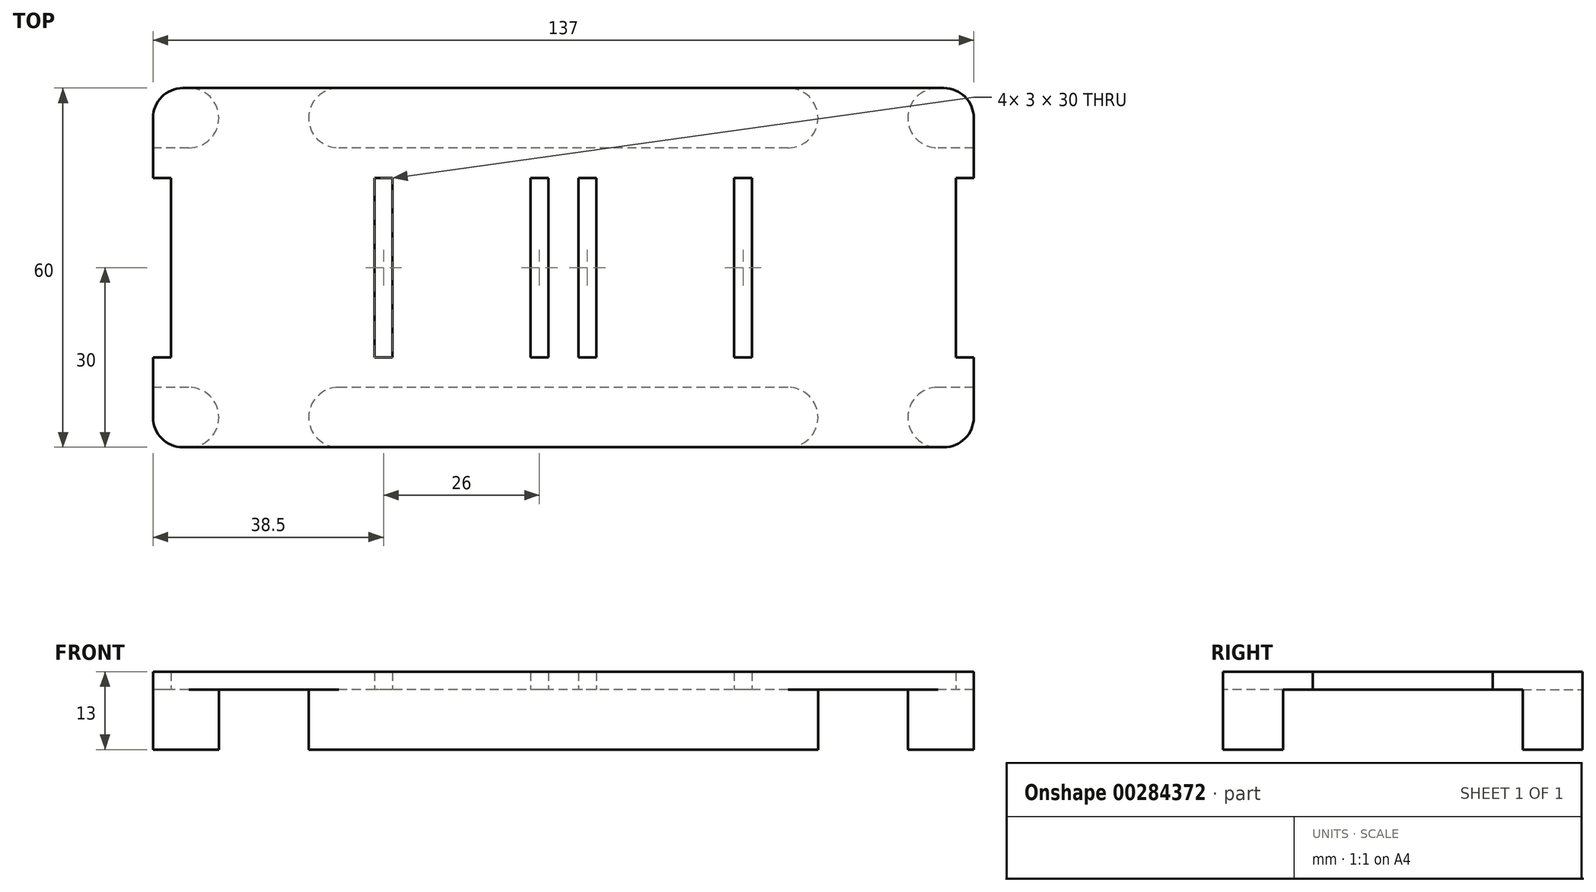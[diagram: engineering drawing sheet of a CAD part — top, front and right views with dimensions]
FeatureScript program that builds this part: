
annotation { "Feature Type Name" : "Feature", "Feature Type Description" : "" }
export const myFeature = defineFeature(function(context is Context, id is Id, definition is map)
    precondition{}
    {
        {
            var Q0;
            Q0=qCreatedBy(makeId("Top.planeOp"),FACE);
            var sketch = newSketch(context, id + "F0", { "sketchPlane" : qUnion([Q0])});
            skLineSegment(sketch, "E0.bottom", {"start": v(75, -30) * mm, "end": v(-75, -30) * mm});
            skLineSegment(sketch, "E0.top", {"start": v(75, 30) * mm, "end": v(-75, 30) * mm});
            skLineSegment(sketch, "E0.left", {"start": v(75, -30) * mm, "end": v(75, 30) * mm});
            skLineSegment(sketch, "E0.right", {"start": v(-75, -30) * mm, "end": v(-75, 30) * mm});
            skPoint(sketch, "E0.middle", {"position": v(0, 0) * mm});
            skSolve(sketch);
        }
        {
            var Q0;
            Q0 = qSketchRegion(id + "F0", true);
            extrude(context, id + "F1", {"entities" : qUnion([Q0]), "depth" : 3 * mm});
        }
        {
            var Q0;
            Q0=qCreatedBy(makeId("Top.planeOp"),FACE);
            var sketch = newSketch(context, id + "F2", { "sketchPlane" : qUnion([Q0])});
            skLineSegment(sketch, "E1.bottom", {"start": v(-2.5, -15) * mm, "end": v(-5.5, -15) * mm});
            skLineSegment(sketch, "E1.top", {"start": v(-2.5, 15) * mm, "end": v(-5.5, 15) * mm});
            skLineSegment(sketch, "E1.left", {"start": v(-2.5, -15) * mm, "end": v(-2.5, 15) * mm});
            skLineSegment(sketch, "E1.right", {"start": v(-5.5, -15) * mm, "end": v(-5.5, 15) * mm});
            skPoint(sketch, "E1.middle", {"position": v(-4, 0) * mm});
            skLineSegment(sketch, "E2.bottom", {"start": v(5.5, -15) * mm, "end": v(2.5, -15) * mm});
            skLineSegment(sketch, "E2.top", {"start": v(5.5, 15) * mm, "end": v(2.5, 15) * mm});
            skLineSegment(sketch, "E2.left", {"start": v(5.5, -15) * mm, "end": v(5.5, 15) * mm});
            skLineSegment(sketch, "E2.right", {"start": v(2.5, -15) * mm, "end": v(2.5, 15) * mm});
            skPoint(sketch, "E2.middle", {"position": v(4, 0) * mm});
            skLineSegment(sketch, "E3.bottom", {"start": v(68.5, -15) * mm, "end": v(65.5, -15) * mm});
            skLineSegment(sketch, "E3.top", {"start": v(68.5, 15) * mm, "end": v(65.5, 15) * mm});
            skLineSegment(sketch, "E3.left", {"start": v(68.5, -15) * mm, "end": v(68.5, 15) * mm});
            skLineSegment(sketch, "E3.right", {"start": v(65.5, -15) * mm, "end": v(65.5, 15) * mm});
            skPoint(sketch, "E3.middle", {"position": v(67, 0) * mm});
            skLineSegment(sketch, "E4.bottom", {"start": v(-65.5, -15) * mm, "end": v(-68.5, -15) * mm});
            skLineSegment(sketch, "E4.top", {"start": v(-65.5, 15) * mm, "end": v(-68.5, 15) * mm});
            skLineSegment(sketch, "E4.left", {"start": v(-65.5, -15) * mm, "end": v(-65.5, 15) * mm});
            skLineSegment(sketch, "E4.right", {"start": v(-68.5, -15) * mm, "end": v(-68.5, 15) * mm});
            skPoint(sketch, "E4.middle", {"position": v(-67, 0) * mm});
            skLineSegment(sketch, "E5.bottom", {"start": v(-28.5, -15) * mm, "end": v(-31.5, -15) * mm});
            skLineSegment(sketch, "E5.top", {"start": v(-28.5, 15) * mm, "end": v(-31.5, 15) * mm});
            skLineSegment(sketch, "E5.left", {"start": v(-28.5, -15) * mm, "end": v(-28.5, 15) * mm});
            skLineSegment(sketch, "E5.right", {"start": v(-31.5, -15) * mm, "end": v(-31.5, 15) * mm});
            skPoint(sketch, "E5.middle", {"position": v(-30, 0) * mm});
            skLineSegment(sketch, "E6.bottom", {"start": v(31.5, -15) * mm, "end": v(28.5, -15) * mm});
            skLineSegment(sketch, "E6.top", {"start": v(31.5, 15) * mm, "end": v(28.5, 15) * mm});
            skLineSegment(sketch, "E6.left", {"start": v(31.5, -15) * mm, "end": v(31.5, 15) * mm});
            skLineSegment(sketch, "E6.right", {"start": v(28.5, -15) * mm, "end": v(28.5, 15) * mm});
            skPoint(sketch, "E6.middle", {"position": v(30, 0) * mm});
            skSolve(sketch);
        }
        {
            var Q0;
            Q0 = qSketchRegion(id + "F2", true);
            extrude(context, id + "F3", {"entities" : qUnion([Q0]), "operationType" : NewBodyOperationType.REMOVE, "depth" : 25 * mm});
        }
        {
            var Q0;
            Q0=qCreatedBy(makeId("Top.planeOp"),FACE);
            var sketch = newSketch(context, id + "F4", { "sketchPlane" : qUnion([Q0])});
            skLineSegment(sketch, "E7", {"start": v(68.5, 30) * mm, "end": v(68.5, -30) * mm});
            skLineSegment(sketch, "E8", {"start": v(68.5, -30) * mm, "end": v(75, -30) * mm});
            skLineSegment(sketch, "E9", {"start": v(75, -30) * mm, "end": v(75, 30) * mm});
            skLineSegment(sketch, "E10", {"start": v(75, 30) * mm, "end": v(68.5, 30) * mm});
            skPoint(sketch, "E11", {"position": v(75, 0) * mm});
            skLineSegment(sketch, "E12", {"start": v(-68.5, 30) * mm, "end": v(-68.5, -30) * mm});
            skLineSegment(sketch, "E13", {"start": v(-68.5, -30) * mm, "end": v(-75, -30) * mm});
            skLineSegment(sketch, "E14", {"start": v(-75, -30) * mm, "end": v(-75, 30) * mm});
            skLineSegment(sketch, "E15", {"start": v(-75, 30) * mm, "end": v(-68.5, 30) * mm});
            skSolve(sketch);
        }
        {
            var Q0;
            Q0 = qSketchRegion(id + "F4", true);
            extrude(context, id + "F5", {"entities" : qUnion([Q0]), "operationType" : NewBodyOperationType.REMOVE, "depth" : 25 * mm});
        }
        {
            var Q0;
            Q0=qCreatedBy(makeId("Top.planeOp"),FACE);
            var sketch = newSketch(context, id + "F6", { "sketchPlane" : qUnion([Q0])});
            skLineSegment(sketch, "E16.bottom", {"start": v(42.5, 20) * mm, "end": v(-42.5, 20) * mm});
            skLineSegment(sketch, "E16.top", {"start": v(42.5, 30) * mm, "end": v(-42.5, 30) * mm});
            skLineSegment(sketch, "E16.left", {"start": v(42.5, 20) * mm, "end": v(42.5, 30) * mm});
            skLineSegment(sketch, "E16.right", {"start": v(-42.5, 20) * mm, "end": v(-42.5, 30) * mm});
            skPoint(sketch, "E16.middle", {"position": v(0, 25) * mm});
            skLineSegment(sketch, "E17.bottom", {"start": v(42.5, -30) * mm, "end": v(-42.5, -30) * mm});
            skLineSegment(sketch, "E17.top", {"start": v(42.5, -20) * mm, "end": v(-42.5, -20) * mm});
            skLineSegment(sketch, "E17.left", {"start": v(42.5, -30) * mm, "end": v(42.5, -20) * mm});
            skLineSegment(sketch, "E17.right", {"start": v(-42.5, -30) * mm, "end": v(-42.5, -20) * mm});
            skPoint(sketch, "E17.middle", {"position": v(0, -25) * mm});
            skLineSegment(sketch, "E18.bottom", {"start": v(68.5, 20) * mm, "end": v(57.5, 20) * mm});
            skLineSegment(sketch, "E18.top", {"start": v(68.5, 30) * mm, "end": v(57.5, 30) * mm});
            skLineSegment(sketch, "E18.left", {"start": v(68.5, 20) * mm, "end": v(68.5, 30) * mm});
            skLineSegment(sketch, "E18.right", {"start": v(57.5, 20) * mm, "end": v(57.5, 30) * mm});
            skPoint(sketch, "E18.middle", {"position": v(63, 25) * mm});
            skLineSegment(sketch, "E19.bottom", {"start": v(68.5, -30) * mm, "end": v(57.5, -30) * mm});
            skLineSegment(sketch, "E19.top", {"start": v(68.5, -20) * mm, "end": v(57.5, -20) * mm});
            skLineSegment(sketch, "E19.left", {"start": v(68.5, -30) * mm, "end": v(68.5, -20) * mm});
            skLineSegment(sketch, "E19.right", {"start": v(57.5, -30) * mm, "end": v(57.5, -20) * mm});
            skPoint(sketch, "E19.middle", {"position": v(63, -25) * mm});
            skLineSegment(sketch, "E20.bottom", {"start": v(-57.5, -30) * mm, "end": v(-68.5, -30) * mm});
            skLineSegment(sketch, "E20.top", {"start": v(-57.5, -20) * mm, "end": v(-68.5, -20) * mm});
            skLineSegment(sketch, "E20.left", {"start": v(-57.5, -30) * mm, "end": v(-57.5, -20) * mm});
            skLineSegment(sketch, "E20.right", {"start": v(-68.5, -30) * mm, "end": v(-68.5, -20) * mm});
            skPoint(sketch, "E20.middle", {"position": v(-63, -25) * mm});
            skLineSegment(sketch, "E21.bottom", {"start": v(-57.5, 20) * mm, "end": v(-68.5, 20) * mm});
            skLineSegment(sketch, "E21.top", {"start": v(-57.5, 30) * mm, "end": v(-68.5, 30) * mm});
            skLineSegment(sketch, "E21.left", {"start": v(-57.5, 20) * mm, "end": v(-57.5, 30) * mm});
            skLineSegment(sketch, "E21.right", {"start": v(-68.5, 20) * mm, "end": v(-68.5, 30) * mm});
            skPoint(sketch, "E21.middle", {"position": v(-63, 25) * mm});
            skSolve(sketch);
        }
        {
            var Q0;
            Q0 = qSketchRegion(id + "F6", true);
            extrude(context, id + "F7", {"entities" : qUnion([Q0]), "operationType" : NewBodyOperationType.ADD, "oppositeDirection" : true, "depth" : 10 * mm});
        }
        {
            var Q0;
            Q0=makeQuery(id+"F7.boolean.opBoolean","MERGE",EDGE,{"derivedFrom":[makeQuery(id+"F5.boolean.opBoolean","COPY",EDGE,{"derivedFrom":makeQuery(id+"F5.opExtrude","SWEPT_EDGE",EDGE,{"disambiguationData":[OSD([sQuery(id+"F4.wireOp",EDGE,"E12"),sQuery(id+"F4.wireOp",EDGE,"E13")])]})}),makeQuery(id+"F7.opExtrude","SWEPT_EDGE",EDGE,{"disambiguationData":[OSD([sQuery(id+"F6.wireOp",EDGE,"E20.bottom"),sQuery(id+"F6.wireOp",EDGE,"E20.right")])]})]});
            var Q1;
            Q1=makeQuery(id+"F7.boolean.opBoolean","MERGE",EDGE,{"derivedFrom":[makeQuery(id+"F5.boolean.opBoolean","COPY",EDGE,{"derivedFrom":makeQuery(id+"F5.opExtrude","SWEPT_EDGE",EDGE,{"disambiguationData":[OSD([sQuery(id+"F4.wireOp",EDGE,"E12"),sQuery(id+"F4.wireOp",EDGE,"E15")])]})}),makeQuery(id+"F7.opExtrude","SWEPT_EDGE",EDGE,{"disambiguationData":[OSD([sQuery(id+"F6.wireOp",EDGE,"E21.top"),sQuery(id+"F6.wireOp",EDGE,"E21.right")])]})]});
            var Q2;
            Q2=makeQuery(id+"F7.boolean.opBoolean","MERGE",EDGE,{"derivedFrom":[makeQuery(id+"F5.boolean.opBoolean","COPY",EDGE,{"derivedFrom":makeQuery(id+"F5.opExtrude","SWEPT_EDGE",EDGE,{"disambiguationData":[OSD([sQuery(id+"F4.wireOp",EDGE,"E7"),sQuery(id+"F4.wireOp",EDGE,"E10")])]})}),makeQuery(id+"F7.opExtrude","SWEPT_EDGE",EDGE,{"disambiguationData":[OSD([sQuery(id+"F6.wireOp",EDGE,"E18.top"),sQuery(id+"F6.wireOp",EDGE,"E18.left")])]})]});
            var Q3;
            Q3=makeQuery(id+"F7.boolean.opBoolean","MERGE",EDGE,{"derivedFrom":[makeQuery(id+"F5.boolean.opBoolean","COPY",EDGE,{"derivedFrom":makeQuery(id+"F5.opExtrude","SWEPT_EDGE",EDGE,{"disambiguationData":[OSD([sQuery(id+"F4.wireOp",EDGE,"E7"),sQuery(id+"F4.wireOp",EDGE,"E8")])]})}),makeQuery(id+"F7.opExtrude","SWEPT_EDGE",EDGE,{"disambiguationData":[OSD([sQuery(id+"F6.wireOp",EDGE,"E19.bottom"),sQuery(id+"F6.wireOp",EDGE,"E19.left")])]})]});
            var Q4;
            Q4=makeQuery(id+"F7.opExtrude","SWEPT_EDGE",EDGE,{"disambiguationData":[OSD([sQuery(id+"F6.wireOp",EDGE,"E16.top"),sQuery(id+"F6.wireOp",EDGE,"E16.left")])]});
            var Q5;
            Q5=makeQuery(id+"F7.opExtrude","SWEPT_EDGE",EDGE,{"disambiguationData":[OSD([sQuery(id+"F6.wireOp",EDGE,"E16.bottom"),sQuery(id+"F6.wireOp",EDGE,"E16.left")])]});
            var Q6;
            Q6=makeQuery(id+"F7.opExtrude","SWEPT_EDGE",EDGE,{"disambiguationData":[OSD([sQuery(id+"F6.wireOp",EDGE,"E17.top"),sQuery(id+"F6.wireOp",EDGE,"E17.left")])]});
            var Q7;
            Q7=makeQuery(id+"F7.opExtrude","SWEPT_EDGE",EDGE,{"disambiguationData":[OSD([sQuery(id+"F6.wireOp",EDGE,"E17.bottom"),sQuery(id+"F6.wireOp",EDGE,"E17.left")])]});
            var Q8;
            Q8=makeQuery(id+"F7.opExtrude","SWEPT_EDGE",EDGE,{"disambiguationData":[OSD([sQuery(id+"F6.wireOp",EDGE,"E18.top"),sQuery(id+"F6.wireOp",EDGE,"E18.right")])]});
            var Q9;
            Q9=makeQuery(id+"F7.opExtrude","SWEPT_EDGE",EDGE,{"disambiguationData":[OSD([sQuery(id+"F6.wireOp",EDGE,"E18.bottom"),sQuery(id+"F6.wireOp",EDGE,"E18.right")])]});
            var Q10;
            Q10=makeQuery(id+"F7.opExtrude","SWEPT_EDGE",EDGE,{"disambiguationData":[OSD([sQuery(id+"F6.wireOp",EDGE,"E19.top"),sQuery(id+"F6.wireOp",EDGE,"E19.right")])]});
            var Q11;
            Q11=makeQuery(id+"F7.opExtrude","SWEPT_EDGE",EDGE,{"disambiguationData":[OSD([sQuery(id+"F6.wireOp",EDGE,"E19.bottom"),sQuery(id+"F6.wireOp",EDGE,"E19.right")])]});
            var Q12;
            Q12=makeQuery(id+"F7.opExtrude","SWEPT_EDGE",EDGE,{"disambiguationData":[OSD([sQuery(id+"F6.wireOp",EDGE,"E16.top"),sQuery(id+"F6.wireOp",EDGE,"E16.right")])]});
            var Q13;
            Q13=makeQuery(id+"F7.opExtrude","SWEPT_EDGE",EDGE,{"disambiguationData":[OSD([sQuery(id+"F6.wireOp",EDGE,"E16.bottom"),sQuery(id+"F6.wireOp",EDGE,"E16.right")])]});
            var Q14;
            Q14=makeQuery(id+"F7.opExtrude","SWEPT_EDGE",EDGE,{"disambiguationData":[OSD([sQuery(id+"F6.wireOp",EDGE,"E17.top"),sQuery(id+"F6.wireOp",EDGE,"E17.right")])]});
            var Q15;
            Q15=makeQuery(id+"F7.opExtrude","SWEPT_EDGE",EDGE,{"disambiguationData":[OSD([sQuery(id+"F6.wireOp",EDGE,"E17.bottom"),sQuery(id+"F6.wireOp",EDGE,"E17.right")])]});
            var Q16;
            Q16=makeQuery(id+"F7.opExtrude","SWEPT_EDGE",EDGE,{"disambiguationData":[OSD([sQuery(id+"F6.wireOp",EDGE,"E21.top"),sQuery(id+"F6.wireOp",EDGE,"E21.left")])]});
            var Q17;
            Q17=makeQuery(id+"F7.opExtrude","SWEPT_EDGE",EDGE,{"disambiguationData":[OSD([sQuery(id+"F6.wireOp",EDGE,"E21.bottom"),sQuery(id+"F6.wireOp",EDGE,"E21.left")])]});
            var Q18;
            Q18=makeQuery(id+"F7.opExtrude","SWEPT_EDGE",EDGE,{"disambiguationData":[OSD([sQuery(id+"F6.wireOp",EDGE,"E20.top"),sQuery(id+"F6.wireOp",EDGE,"E20.left")])]});
            var Q19;
            Q19=makeQuery(id+"F7.opExtrude","SWEPT_EDGE",EDGE,{"disambiguationData":[OSD([sQuery(id+"F6.wireOp",EDGE,"E20.bottom"),sQuery(id+"F6.wireOp",EDGE,"E20.left")])]});
            fillet(context, id + "F8", {"entities" : qUnion([Q0, Q1, Q2, Q3, Q4, Q5, Q6, Q7, Q8, Q9, Q10, Q11, Q12, Q13, Q14, Q15, Q16, Q17, Q18, Q19]), "radius" : 5 * mm, "tangentPropagation" : true, "allowEdgeOverflow" : false});
        }
    });
